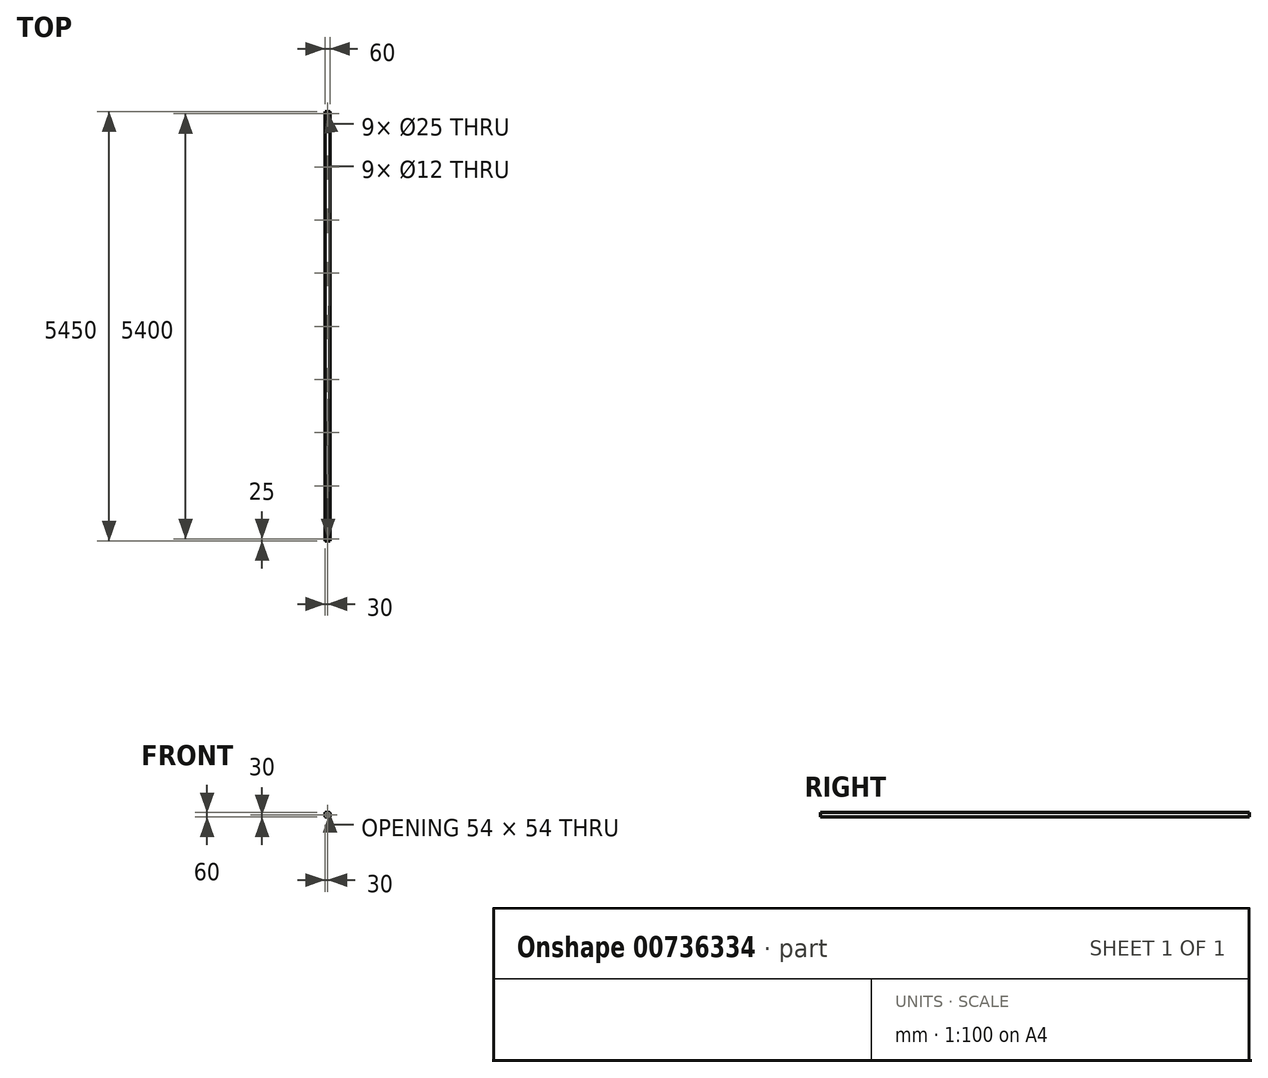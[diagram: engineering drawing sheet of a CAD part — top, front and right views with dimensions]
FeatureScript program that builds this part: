
annotation { "Feature Type Name" : "Feature", "Feature Type Description" : "" }
export const myFeature = defineFeature(function(context is Context, id is Id, definition is map)
    precondition{}
    {
        {
            var Q0;
            Q0=qCreatedBy(makeId("Front.planeOp"),FACE);
            var sketch = newSketch(context, id + "F0", { "sketchPlane" : qUnion([Q0])});
            skLineSegment(sketch, "E0.bottom", {"start": v(-25, 30) * mm, "end": v(25, 30) * mm});
            skLineSegment(sketch, "E0.top", {"start": v(-25, -30) * mm, "end": v(25, -30) * mm});
            skLineSegment(sketch, "E0.left", {"start": v(-30, 25) * mm, "end": v(-30, -25) * mm});
            skLineSegment(sketch, "E0.right", {"start": v(30, 25) * mm, "end": v(30, -25) * mm});
            skPoint(sketch, "E1.visualSharp", {"position": v(-30, 30) * mm});
            skArc(sketch, "E1.filletArc", {"start": v(-25, 30) * mm, "mid": v(-28.54, 28.54) * mm, "end": v(-30, 25) * mm});
            skPoint(sketch, "E2.visualSharp", {"position": v(30, 30) * mm});
            skArc(sketch, "E2.filletArc", {"start": v(30, 25) * mm, "mid": v(28.54, 28.54) * mm, "end": v(25, 30) * mm});
            skPoint(sketch, "E3.visualSharp", {"position": v(30, -30) * mm});
            skArc(sketch, "E3.filletArc", {"start": v(25, -30) * mm, "mid": v(28.54, -28.54) * mm, "end": v(30, -25) * mm});
            skPoint(sketch, "E4.visualSharp", {"position": v(-30, -30) * mm});
            skArc(sketch, "E4.filletArc", {"start": v(-30, -25) * mm, "mid": v(-28.54, -28.54) * mm, "end": v(-25, -30) * mm});
            skLineSegment(sketch, "E5.0", {"start": v(-27, 25) * mm, "end": v(-27, -25) * mm});
            skLineSegment(sketch, "E5.1", {"start": v(-25, 27) * mm, "end": v(25, 27) * mm});
            skLineSegment(sketch, "E6.0", {"start": v(27, 25) * mm, "end": v(27, -25) * mm});
            skLineSegment(sketch, "E7.0", {"start": v(-25, -27) * mm, "end": v(25, -27) * mm});
            skArc(sketch, "E8.filletArc", {"start": v(-27, -25) * mm, "mid": v(-26.41, -26.41) * mm, "end": v(-25, -27) * mm});
            skArc(sketch, "E9.filletArc", {"start": v(25, -27) * mm, "mid": v(26.41, -26.41) * mm, "end": v(27, -25) * mm});
            skArc(sketch, "E10.filletArc", {"start": v(27, 25) * mm, "mid": v(26.41, 26.41) * mm, "end": v(25, 27) * mm});
            skPoint(sketch, "E11.visualSharp", {"position": v(-27, 27) * mm});
            skArc(sketch, "E11.filletArc", {"start": v(-25, 27) * mm, "mid": v(-26.41, 26.41) * mm, "end": v(-27, 25) * mm});
            skSolve(sketch);
        }
        {
            var Q0;
            Q0 = qSketchRegion(id + "F0", true);
            extrude(context, id + "F1", {"entities" : qUnion([Q0]), "depth" : 5450 * mm, "offsetDistance" : 25 * mm});
        }
        {
            var Q0;
            Q0=makeQuery(id+"F1.opExtrude","SWEPT_FACE",FACE,{"disambiguationData":[OSD([sQuery(id+"F0.wireOp",EDGE,"E0.bottom")])]});
            var sketch = newSketch(context, id + "F2", { "sketchPlane" : qUnion([Q0])});
            skCircle(sketch, "E12", {"center": v(0, -5425) * mm, "radius": 12.5 * mm});
            skCircle(sketch, "E13.0.1.0", {"center": v(0, -4750) * mm, "radius": 12.5 * mm});
            skCircle(sketch, "E13.0.2.0", {"center": v(0, -4075) * mm, "radius": 12.5 * mm});
            skCircle(sketch, "E13.0.3.0", {"center": v(0, -3400) * mm, "radius": 12.5 * mm});
            skCircle(sketch, "E13.0.4.0", {"center": v(0, -2725) * mm, "radius": 12.5 * mm});
            skCircle(sketch, "E13.0.5.0", {"center": v(0, -2050) * mm, "radius": 12.5 * mm});
            skCircle(sketch, "E13.0.6.0", {"center": v(0, -1375) * mm, "radius": 12.5 * mm});
            skCircle(sketch, "E13.0.7.0", {"center": v(0, -700) * mm, "radius": 12.5 * mm});
            skCircle(sketch, "E13.0.8.0", {"center": v(0, -25) * mm, "radius": 12.5 * mm});
            skLineSegment(sketch, "E13.direction1", {"start": v(0, -5425) * mm, "end": v(25, -5425) * mm, "construction": true});
            skLineSegment(sketch, "E13.direction2", {"start": v(0, -5425) * mm, "end": v(0, -4750) * mm, "construction": true});
            skSolve(sketch);
        }
        {
            var Q0;
            Q0 = qSketchRegion(id + "F2", true);
            extrude(context, id + "F3", {"entities" : qUnion([Q0]), "operationType" : NewBodyOperationType.REMOVE, "oppositeDirection" : true, "depth" : 4 * mm, "offsetDistance" : 25 * mm});
        }
        {
            var Q0;
            Q0=makeQuery(id+"F1.opExtrude","SWEPT_FACE",FACE,{"disambiguationData":[OSD([sQuery(id+"F0.wireOp",EDGE,"E0.top")])]});
            var sketch = newSketch(context, id + "F4", { "sketchPlane" : qUnion([Q0])});
            skCircle(sketch, "E14", {"center": v(0, 25) * mm, "radius": 6 * mm});
            skCircle(sketch, "E15.0.1.0", {"center": v(0, 700) * mm, "radius": 6 * mm});
            skCircle(sketch, "E15.0.2.0", {"center": v(0, 1375) * mm, "radius": 6 * mm});
            skCircle(sketch, "E15.0.3.0", {"center": v(0, 2050) * mm, "radius": 6 * mm});
            skCircle(sketch, "E15.0.4.0", {"center": v(0, 2725) * mm, "radius": 6 * mm});
            skCircle(sketch, "E15.0.5.0", {"center": v(0, 3400) * mm, "radius": 6 * mm});
            skCircle(sketch, "E15.0.6.0", {"center": v(0, 4075) * mm, "radius": 6 * mm});
            skCircle(sketch, "E15.0.7.0", {"center": v(0, 4750) * mm, "radius": 6 * mm});
            skCircle(sketch, "E15.0.8.0", {"center": v(0, 5425) * mm, "radius": 6 * mm});
            skLineSegment(sketch, "E15.direction1", {"start": v(0, 25) * mm, "end": v(25, 25) * mm, "construction": true});
            skLineSegment(sketch, "E15.direction2", {"start": v(0, 25) * mm, "end": v(0, 700) * mm, "construction": true});
            skSolve(sketch);
        }
        {
            var Q0;
            Q0 = qSketchRegion(id + "F4", true);
            extrude(context, id + "F5", {"entities" : qUnion([Q0]), "operationType" : NewBodyOperationType.REMOVE, "oppositeDirection" : true, "depth" : 4 * mm, "offsetDistance" : 25 * mm});
        }
    });
